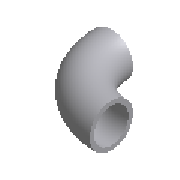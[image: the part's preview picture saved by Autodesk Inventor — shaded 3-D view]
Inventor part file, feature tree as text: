
AUTODESK INVENTOR PART (.ipt)
format: ipt  version: 2025 (Build 290162010, 162A)  size: 185,344 bytes
history: native  units: mm (DEFAULTED — no unit token found)
features: other x4, sweep x1
ambient origin geometry x8: Origin, YZ Plane, XZ Plane, XY Plane, X Axis, Y Axis, Z Axis, Center Point
bodies: Solid1 (feature_tree)
feature tree (5):
  sweep  "Sweep1"
  other  "Work Point1"
  other  "Work Point2"
  other  "Work Axis1"
  other  "Work Axis2"
